# Revit family: Pendelgelenk M12-M12
name_source: partatom
category: HLS-Bauteile
revit_build: Autodesk Revit 2017 (Build: 20190507_1515(x64)
units: mm (PartAtom-declared; Revit-internal decimal feet)

## family parameters
Arbeitsebenenbasiert = Ja
Beim Laden mit Abzugskörper schneiden = Nein
Bemaßung runder Anschluss = Durchmesser verwenden
Gemeinsam genutzt = Ja
Immer vertikal = Ja
Raumberechnungspunkt = Nein
Teiletyp = Normal

## types (1)
- Pendelgelenk M12/M12
    Artikelnummer = 0788128
    EAN = 4250928418968
    Fabrikat = MEFA
    Firma = MEFA Befestigungs- und Montagesysteme GmbH
    Gewicht = 0.13 kg
    Gewicht pro Bauteil = 0.13 kg
    Gewinde = M12-M12
    Gewindetyp = IG-IG
    Höhe = 90 mm
    Kurztext1 = Pendelgelenk 15°
    Kurztext2 = IG-IG M12-M12
    Länge Gewinde = 0 mm  [stored 0 ft]
    Material = Stahl
    Mengeneinheit = St
    Oberflaeche = galvanisch verzinkt
    Pendelwinkel = 15
    Vorgabe-Ansicht = 1219 mm
    max. zul. Last = 5.00 kN
    vpe = 50 St

note: [stored X ft] marks values corroborated as IEEE doubles in the binary element streams (Revit-internal decimal feet)
